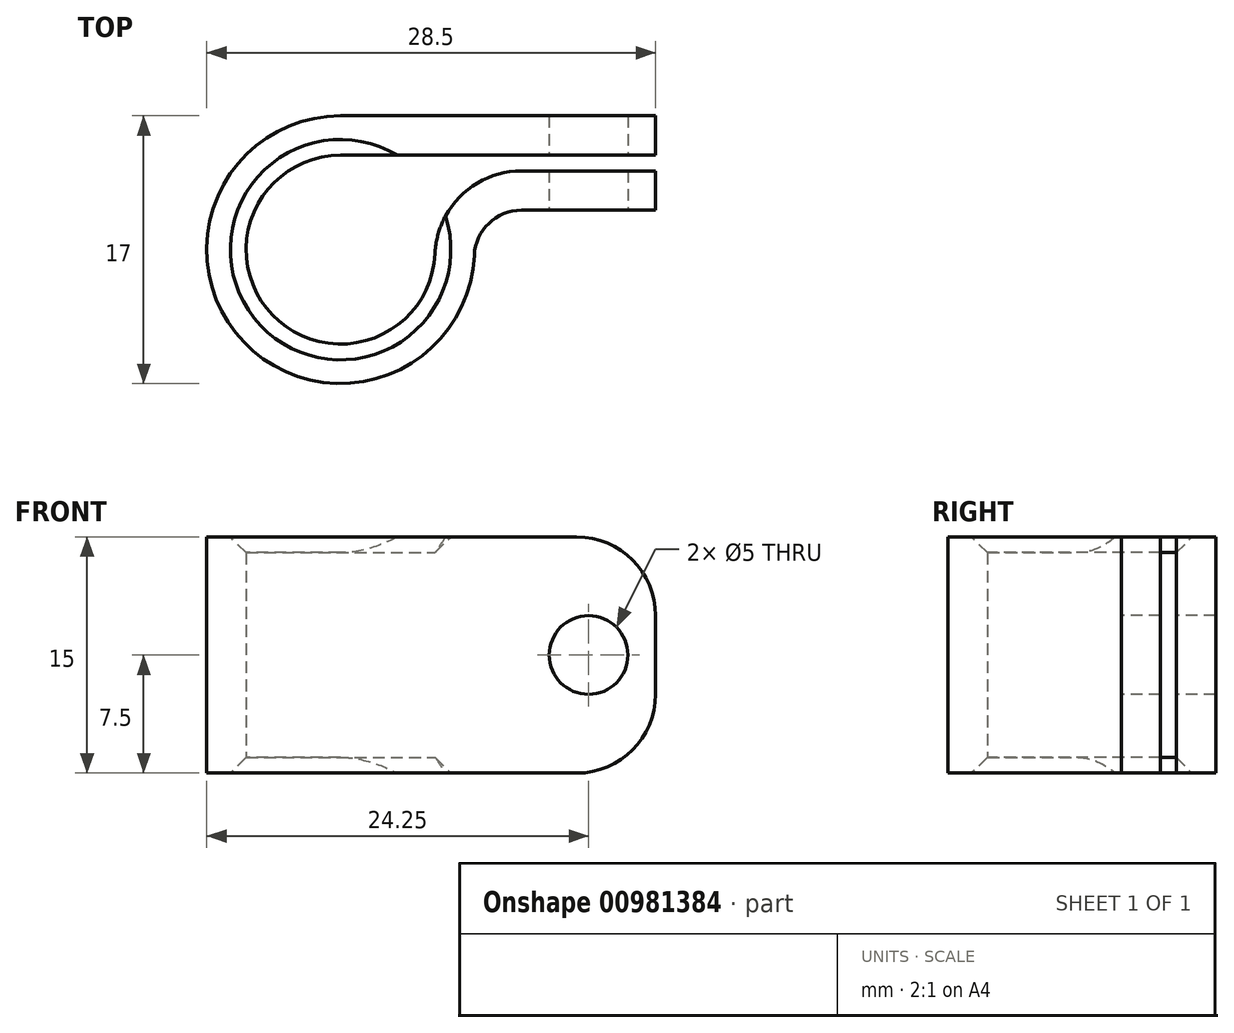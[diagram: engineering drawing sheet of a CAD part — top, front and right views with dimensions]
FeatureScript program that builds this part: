
annotation { "Feature Type Name" : "Feature", "Feature Type Description" : "" }
export const myFeature = defineFeature(function(context is Context, id is Id, definition is map)
    precondition{}
    {
        {
            var Q0;
            Q0=qCreatedBy(makeId("Top.planeOp"),FACE);
            var sketch = newSketch(context, id + "F0", { "sketchPlane" : qUnion([Q0])});
            skCircle(sketch, "E0", {"center": v(0, 0) * mm, "radius": 6 * mm});
            skArc(sketch, "E1", {"start": v(0, 8.5) * mm, "mid": v(-8.5, 0) * mm, "end": v(0, -8.5) * mm});
            skLineSegment(sketch, "E2", {"start": v(0, -8.5) * mm, "end": v(20, -8.5) * mm});
            skLineSegment(sketch, "E3", {"start": v(0, 8.5) * mm, "end": v(20, 8.5) * mm});
            skLineSegment(sketch, "E4", {"start": v(20, 8.5) * mm, "end": v(20, -8.5) * mm});
            skSolve(sketch);
        }
        {
            var Q0;
            Q0=qSketchRegion(id+"F0",true);
            extrude(context, id + "F1", {"entities" : qUnion([Q0]), "endBound" : BoundingType.SYMMETRIC, "depth" : 15 * mm, "offsetDistance" : 25 * mm, "hasSecondDirection" : true, "secondDirectionOppositeDirection" : true, "secondDirectionDepth" : 15 * mm});
        }
        {
            var Q0;
            Q0=makeQuery(id+"F1.opExtrude","CAP_EDGE",EDGE,{"disambiguationData":[OSD([sQuery(id+"F0.wireOp",EDGE,"E0")])],"isStart":false});
            chamfer(context, id + "F2", {"entities" : qUnion([Q0]), "width" : 1 * mm, "tangentPropagation" : true});
        }
        {
            var Q0;
            Q0=makeQuery(id+"F1.opExtrude","CAP_EDGE",EDGE,{"disambiguationData":[OSD([sQuery(id+"F0.wireOp",EDGE,"E0")])],"isStart":true});
            chamfer(context, id + "F3", {"entities" : qUnion([Q0]), "width" : 1 * mm, "tangentPropagation" : true});
        }
        {
            var Q0;
            Q0=makeQuery(id+"F1.opExtrude","CAP_FACE",FACE,{"disambiguationData":[OSD([sQuery(id+"F0.wireOp",EDGE,"E0"),sQuery(id+"F0.wireOp",EDGE,"E1"),sQuery(id+"F0.wireOp",EDGE,"E2"),sQuery(id+"F0.wireOp",EDGE,"E3"),sQuery(id+"F0.wireOp",EDGE,"E4")])],"isStart":false});
            var sketch = newSketch(context, id + "F4", { "sketchPlane" : qUnion([Q0])});
            skArc(sketch, "E5.0", {"start": v(0, -8.5) * mm, "mid": v(6.84, -5.05) * mm, "end": v(8.12, 2.5) * mm});
            skLineSegment(sketch, "E6", {"start": v(20, 2.5) * mm, "end": v(8.12, 2.5) * mm});
            skPoint(sketch, "E7.orphan", {"position": v(0, -8.5) * mm});
            skLineSegment(sketch, "E8.0", {"start": v(0, -8.5) * mm, "end": v(20, -8.5) * mm});
            skPoint(sketch, "E9.orphan", {"position": v(0, 8.5) * mm});
            skLineSegment(sketch, "E10.trimOffspring", {"start": v(20, 2.5) * mm, "end": v(20, -8.5) * mm});
            skPoint(sketch, "E11.0.start.orphan", {"position": v(20, 8.5) * mm});
            skSolve(sketch);
        }
        {
            var Q0;
            Q0 = qSketchRegion(id + "F4", true);
            extrude(context, id + "F5", {"entities" : qUnion([Q0]), "operationType" : NewBodyOperationType.REMOVE, "endBound" : BoundingType.THROUGH_ALL, "depth" : 25 * mm, "offsetDistance" : 25 * mm, "hasSecondDirection" : true, "secondDirectionBound" : SecondDirectionBoundingType.THROUGH_ALL, "secondDirectionOppositeDirection" : true, "secondDirectionDepth" : 25 * mm});
        }
        {
            var Q0;
            Q0=makeQuery(id+"F5.boolean.opBoolean","COPY",EDGE,{"derivedFrom":makeQuery(id+"F5.opExtrude","SWEPT_EDGE",EDGE,{"disambiguationData":[OSD([sQuery(id+"F4.wireOp",EDGE,"E5.0"),sQuery(id+"F4.wireOp",EDGE,"E6")])]})});
            fillet(context, id + "F6", {"entities" : qUnion([Q0]), "radius" : 3 * mm, "tangentPropagation" : true, "allowEdgeOverflow" : false});
        }
        {
            var Q0;
            Q0=makeQuery(id+"F1.opExtrude","CAP_FACE",FACE,{"disambiguationData":[OSD([sQuery(id+"F0.wireOp",EDGE,"E0"),sQuery(id+"F0.wireOp",EDGE,"E1"),sQuery(id+"F0.wireOp",EDGE,"E2"),sQuery(id+"F0.wireOp",EDGE,"E3"),sQuery(id+"F0.wireOp",EDGE,"E4")])],"isStart":false});
            var sketch = newSketch(context, id + "F7", { "sketchPlane" : qUnion([Q0])});
            skLineSegment(sketch, "E12.bottom", {"start": v(20, 6) * mm, "end": v(0, 6) * mm});
            skLineSegment(sketch, "E12.top", {"start": v(20, 5) * mm, "end": v(0, 5) * mm});
            skLineSegment(sketch, "E12.left", {"start": v(20, 6) * mm, "end": v(20, 5) * mm});
            skLineSegment(sketch, "E12.right", {"start": v(0, 6) * mm, "end": v(0, 5) * mm});
            skSolve(sketch);
        }
        {
            var Q0;
            Q0 = qSketchRegion(id + "F7", true);
            extrude(context, id + "F8", {"entities" : qUnion([Q0]), "operationType" : NewBodyOperationType.REMOVE, "endBound" : BoundingType.THROUGH_ALL, "oppositeDirection" : true, "depth" : 25 * mm, "offsetDistance" : 25 * mm});
        }
        {
            var Q0;
            Q0=makeQuery(id+"F8.boolean.opBoolean","INTERSECT",EDGE,{"derivedFrom":[makeQuery(id+"F1.opExtrude","SWEPT_FACE",FACE,{"disambiguationData":[OSD([sQuery(id+"F0.wireOp",EDGE,"E0")])]}),makeQuery(id+"F8.opExtrude","SWEPT_FACE",FACE,{"disambiguationData":[OSD([sQuery(id+"F7.wireOp",EDGE,"E12.top")])]})]});
            fillet(context, id + "F9", {"entities" : qUnion([Q0]), "radius" : 5.5 * mm, "tangentPropagation" : true, "allowEdgeOverflow" : false});
        }
        {
            var Q0;
            {var subQ0=sQuery(id+"F0.wireOp",EDGE,"E4");var subQ1=sQuery(id+"F0.wireOp",EDGE,"E3");Q0=makeQuery(id+"F8.boolean.opBoolean","SPLIT",EDGE,{"disambiguationData":[TD([makeQuery(id+"F1.opExtrude","SWEPT_FACE",FACE,{"disambiguationData":[OSD([subQ1])]})])],"derivedFrom":makeQuery(id+"F1.opExtrude","CAP_EDGE",EDGE,{"disambiguationData":[OSD([subQ0])],"isStart":true})});}
            var Q1;
            {var subQ0=sQuery(id+"F0.wireOp",EDGE,"E4");Q1=makeQuery(id+"F8.boolean.opBoolean","SPLIT",EDGE,{"disambiguationData":[TD([makeQuery(id+"F5.boolean.opBoolean","COPY",FACE,{"derivedFrom":makeQuery(id+"F5.opExtrude","SWEPT_FACE",FACE,{"disambiguationData":[OSD([sQuery(id+"F4.wireOp",EDGE,"E6")])]})})])],"derivedFrom":makeQuery(id+"F1.opExtrude","CAP_EDGE",EDGE,{"disambiguationData":[OSD([subQ0])],"isStart":false})});}
            var Q2;
            {var subQ0=sQuery(id+"F0.wireOp",EDGE,"E4");var subQ1=sQuery(id+"F0.wireOp",EDGE,"E3");Q2=makeQuery(id+"F8.boolean.opBoolean","SPLIT",EDGE,{"disambiguationData":[TD([makeQuery(id+"F1.opExtrude","SWEPT_FACE",FACE,{"disambiguationData":[OSD([subQ1])]})])],"derivedFrom":makeQuery(id+"F1.opExtrude","CAP_EDGE",EDGE,{"disambiguationData":[OSD([subQ0])],"isStart":false})});}
            var Q3;
            {var subQ0=sQuery(id+"F0.wireOp",EDGE,"E4");Q3=makeQuery(id+"F8.boolean.opBoolean","SPLIT",EDGE,{"disambiguationData":[TD([makeQuery(id+"F5.boolean.opBoolean","COPY",FACE,{"derivedFrom":makeQuery(id+"F5.opExtrude","SWEPT_FACE",FACE,{"disambiguationData":[OSD([sQuery(id+"F4.wireOp",EDGE,"E6")])]})})])],"derivedFrom":makeQuery(id+"F1.opExtrude","CAP_EDGE",EDGE,{"disambiguationData":[OSD([subQ0])],"isStart":true})});}
            fillet(context, id + "F10", {"entities" : qUnion([Q0, Q1, Q2, Q3]), "radius" : 5 * mm, "tangentPropagation" : true, "allowEdgeOverflow" : false});
        }
        {
            var Q0;
            Q0=makeQuery(id+"F5.boolean.opBoolean","COPY",FACE,{"derivedFrom":makeQuery(id+"F5.opExtrude","SWEPT_FACE",FACE,{"disambiguationData":[OSD([sQuery(id+"F4.wireOp",EDGE,"E6")])]})});
            var sketch = newSketch(context, id + "F11", { "sketchPlane" : qUnion([Q0])});
            skPoint(sketch, "E13", {"position": v(15.75, 0) * mm});
            skSolve(sketch);
        }
        {
            var Q0;
            Q0=sQuery(id+"F11.wireOp",VERTEX,"E13");
            var Q1;
            Q1=makeQuery(id+"F1.opExtrude","SWEPT_BODY",BODY,{"disambiguationData":[OSD([sQuery(id+"F0.wireOp",EDGE,"E0"),sQuery(id+"F0.wireOp",EDGE,"E1"),sQuery(id+"F0.wireOp",EDGE,"E2"),sQuery(id+"F0.wireOp",EDGE,"E3"),sQuery(id+"F0.wireOp",EDGE,"E4")])]});
            hole(context, id + "F12", {"style" : HoleStyle.SIMPLE, "endStyle" : HoleEndStyle.THROUGH, "holeDiameter" : 5 * mm, "majorDiameter" : 5 * mm, "isTappedThrough" : true, "tappedDepth" : 12 * mm, "tapClearance" : 3, "locations" : qUnion([Q0]), "scope" : qUnion([Q1])});
        }
    });
